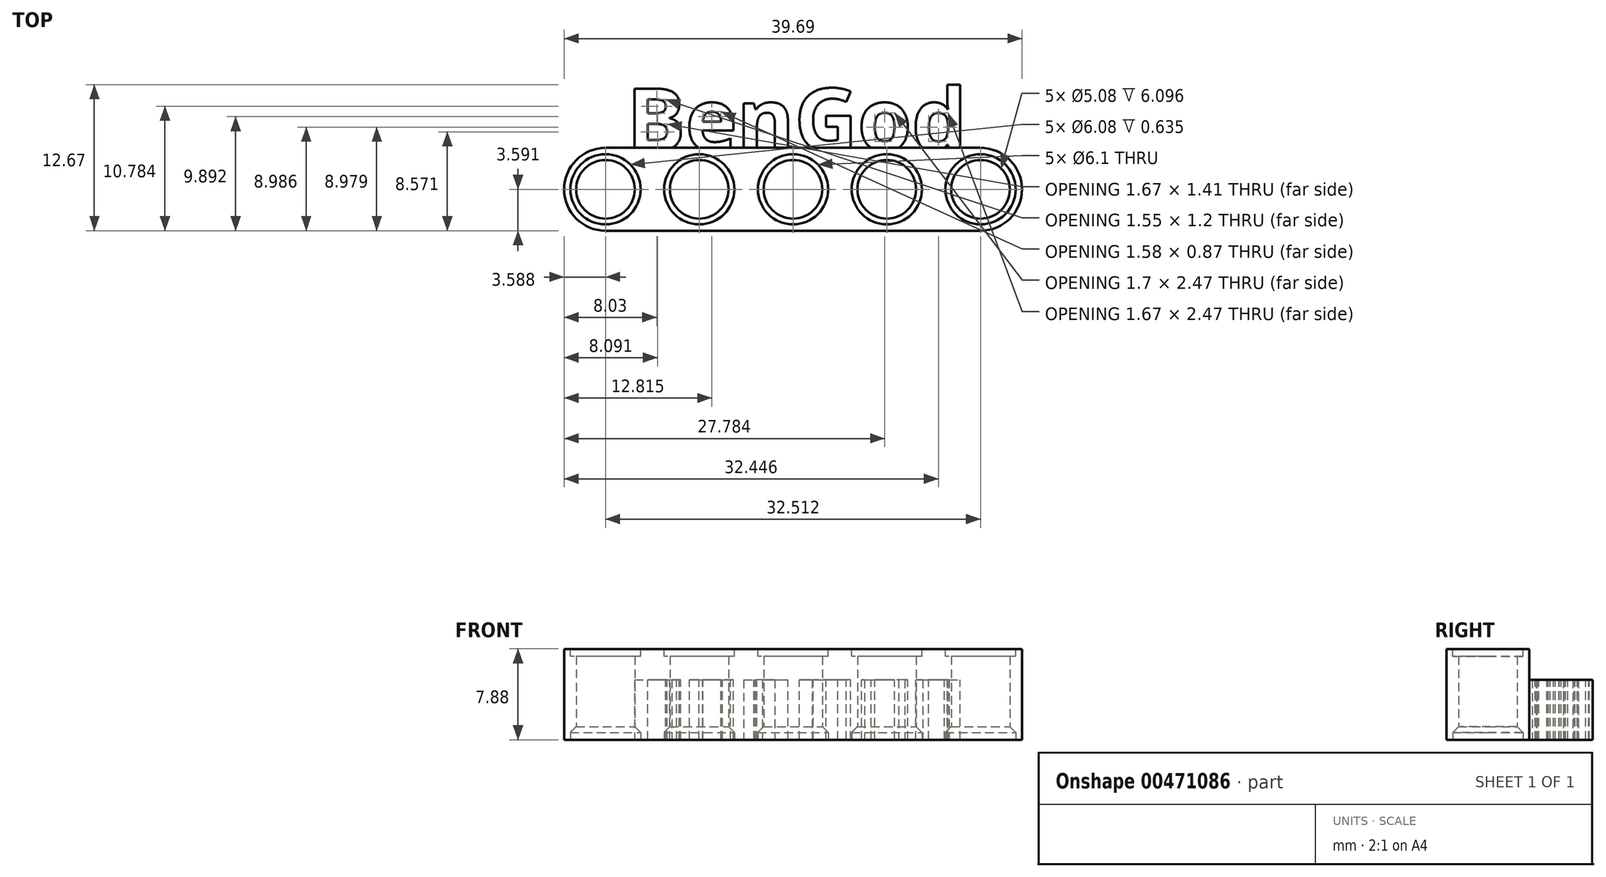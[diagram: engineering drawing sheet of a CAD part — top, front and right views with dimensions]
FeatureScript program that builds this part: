
annotation { "Feature Type Name" : "Feature", "Feature Type Description" : "" }
export const myFeature = defineFeature(function(context is Context, id is Id, definition is map)
    precondition{}
    {
        {
            var Q0;
            Q0=qCreatedBy(makeId("Top.planeOp"),FACE);
            var sketch = newSketch(context, id + "F0", { "sketchPlane" : qUnion([Q0])});
            skCircle(sketch, "E0", {"center": v(-60.84, 14.37) * mm, "radius": 3.6 * mm});
            skCircle(sketch, "E1.1.0.0", {"center": v(-52.71, 14.37) * mm, "radius": 3.6 * mm});
            skCircle(sketch, "E1.2.0.0", {"center": v(-44.59, 14.37) * mm, "radius": 3.6 * mm});
            skCircle(sketch, "E1.3.0.0", {"center": v(-36.46, 14.37) * mm, "radius": 3.6 * mm});
            skLineSegment(sketch, "E1.direction1", {"start": v(-60.84, 14.37) * mm, "end": v(-52.71, 14.37) * mm, "construction": true});
            skCircle(sketch, "E2.0.4.0", {"center": v(-28.33, 14.37) * mm, "radius": 3.6 * mm});
            skLineSegment(sketch, "E3.left", {"start": v(-60.84, 14.37) * mm, "end": v(-60.84, 14.37) * mm});
            skLineSegment(sketch, "E3.right", {"start": v(-28.33, 14.37) * mm, "end": v(-28.33, 14.37) * mm});
            skLineSegment(sketch, "E4.bottom", {"start": v(-60.84, 17.96) * mm, "end": v(-28.33, 17.96) * mm});
            skLineSegment(sketch, "E4.top", {"start": v(-60.84, 10.78) * mm, "end": v(-28.33, 10.78) * mm});
            skCircle(sketch, "E5", {"center": v(-60.84, 14.37) * mm, "radius": 3.05 * mm});
            skCircle(sketch, "E6.1.0.0", {"center": v(-52.71, 14.37) * mm, "radius": 3.05 * mm});
            skCircle(sketch, "E6.2.0.0", {"center": v(-44.59, 14.37) * mm, "radius": 3.05 * mm});
            skCircle(sketch, "E6.3.0.0", {"center": v(-36.46, 14.37) * mm, "radius": 3.05 * mm});
            skCircle(sketch, "E6.4.0.0", {"center": v(-28.33, 14.37) * mm, "radius": 3.05 * mm});
            skCircle(sketch, "E7", {"center": v(-60.84, 14.37) * mm, "radius": 2.54 * mm});
            skCircle(sketch, "E8.1.0.0", {"center": v(-52.71, 14.37) * mm, "radius": 2.54 * mm});
            skCircle(sketch, "E8.2.0.0", {"center": v(-44.59, 14.37) * mm, "radius": 2.54 * mm});
            skCircle(sketch, "E8.3.0.0", {"center": v(-36.46, 14.37) * mm, "radius": 2.54 * mm});
            skCircle(sketch, "E8.4.0.0", {"center": v(-28.33, 14.37) * mm, "radius": 2.54 * mm});
            skSolve(sketch);
        }
        {
            var Q0;
            Q0=makeQuery(id+"F0.imprint","IMPRINT",FACE,{"disambiguationData":[TD([[makeQuery(id+"F0.imprint","IMPRINT",EDGE,{"derivedFrom":sQuery(id+"F0.wireOp",EDGE,"E6.2.0.0")}),1.0]])]});
            var Q1;
            {var subQ0=sQuery(id+"F0.wireOp",EDGE,"E4.bottom");var subQ1=sQuery(id+"F0.wireOp",EDGE,"E0");var subQ2=makeQuery(id+"F0.imprint","INTERSECT",VERTEX,{"derivedFrom":[subQ1,subQ0]});Q1=makeQuery(id+"F0.imprint","IMPRINT",FACE,{"disambiguationData":[TD([[makeQuery(id+"F0.imprint","IMPRINT",EDGE,{"disambiguationData":[TD([[subQ2,1.0]])],"derivedFrom":subQ1}),-1.0]])]});}
            var Q2;
            {var subQ0=sQuery(id+"F0.wireOp",EDGE,"E4.bottom");var subQ1=sQuery(id+"F0.wireOp",EDGE,"E1.1.0.0");var subQ2=makeQuery(id+"F0.imprint","INTERSECT",VERTEX,{"derivedFrom":[subQ1,subQ0]});Q2=makeQuery(id+"F0.imprint","IMPRINT",FACE,{"disambiguationData":[TD([[makeQuery(id+"F0.imprint","IMPRINT",EDGE,{"disambiguationData":[TD([[subQ2,1.0]])],"derivedFrom":subQ1}),-1.0]])]});}
            var Q3;
            Q3=makeQuery(id+"F0.imprint","IMPRINT",FACE,{"disambiguationData":[TD([[makeQuery(id+"F0.imprint","IMPRINT",EDGE,{"derivedFrom":sQuery(id+"F0.wireOp",EDGE,"E6.2.0.0")}),-1.0]])]});
            var Q4;
            Q4=makeQuery(id+"F0.imprint","IMPRINT",FACE,{"disambiguationData":[TD([[makeQuery(id+"F0.imprint","IMPRINT",EDGE,{"derivedFrom":sQuery(id+"F0.wireOp",EDGE,"E6.1.0.0")}),-1.0]])]});
            var Q5;
            Q5=makeQuery(id+"F0.imprint","IMPRINT",FACE,{"disambiguationData":[TD([[makeQuery(id+"F0.imprint","IMPRINT",EDGE,{"derivedFrom":sQuery(id+"F0.wireOp",EDGE,"E6.3.0.0")}),-1.0]])]});
            var Q6;
            Q6=makeQuery(id+"F0.imprint","IMPRINT",FACE,{"disambiguationData":[TD([[makeQuery(id+"F0.imprint","IMPRINT",EDGE,{"derivedFrom":sQuery(id+"F0.wireOp",EDGE,"E6.3.0.0")}),1.0]])]});
            var Q7;
            {var subQ0=sQuery(id+"F0.wireOp",EDGE,"E4.bottom");var subQ1=sQuery(id+"F0.wireOp",EDGE,"E1.3.0.0");var subQ2=makeQuery(id+"F0.imprint","INTERSECT",VERTEX,{"derivedFrom":[subQ1,subQ0]});Q7=makeQuery(id+"F0.imprint","IMPRINT",FACE,{"disambiguationData":[TD([[makeQuery(id+"F0.imprint","IMPRINT",EDGE,{"disambiguationData":[TD([[subQ2,1.0]])],"derivedFrom":subQ1}),-1.0]])]});}
            var Q8;
            Q8=makeQuery(id+"F0.imprint","IMPRINT",FACE,{"disambiguationData":[TD([[makeQuery(id+"F0.imprint","IMPRINT",EDGE,{"derivedFrom":sQuery(id+"F0.wireOp",EDGE,"E6.4.0.0")}),-1.0]])]});
            var Q9;
            Q9=makeQuery(id+"F0.imprint","IMPRINT",FACE,{"disambiguationData":[TD([[makeQuery(id+"F0.imprint","IMPRINT",EDGE,{"derivedFrom":sQuery(id+"F0.wireOp",EDGE,"E6.1.0.0")}),1.0]])]});
            var Q10;
            {var subQ0=sQuery(id+"F0.wireOp",EDGE,"E4.bottom");var subQ1=sQuery(id+"F0.wireOp",EDGE,"E1.2.0.0");var subQ2=makeQuery(id+"F0.imprint","INTERSECT",VERTEX,{"derivedFrom":[subQ1,subQ0]});Q10=makeQuery(id+"F0.imprint","IMPRINT",FACE,{"disambiguationData":[TD([[makeQuery(id+"F0.imprint","IMPRINT",EDGE,{"disambiguationData":[TD([[subQ2,1.0]])],"derivedFrom":subQ1}),-1.0]])]});}
            var Q11;
            Q11=makeQuery(id+"F0.imprint","IMPRINT",FACE,{"disambiguationData":[TD([[makeQuery(id+"F0.imprint","IMPRINT",EDGE,{"derivedFrom":sQuery(id+"F0.wireOp",EDGE,"E6.4.0.0")}),1.0]])]});
            var Q12;
            Q12=makeQuery(id+"F0.imprint","IMPRINT",FACE,{"disambiguationData":[TD([[makeQuery(id+"F0.imprint","IMPRINT",EDGE,{"derivedFrom":sQuery(id+"F0.wireOp",EDGE,"E5")}),-1.0]])]});
            var Q13;
            Q13=makeQuery(id+"F0.imprint","IMPRINT",FACE,{"disambiguationData":[TD([[makeQuery(id+"F0.imprint","IMPRINT",EDGE,{"derivedFrom":sQuery(id+"F0.wireOp",EDGE,"E5")}),1.0]])]});
            extrude(context, id + "F1", {"entities" : qUnion([Q0, Q1, Q2, Q3, Q4, Q5, Q6, Q7, Q8, Q9, Q10, Q11, Q12, Q13]), "endBound" : BoundingType.SYMMETRIC, "depth" : 7.87 * mm});
        }
        {
            var Q0;
            Q0=makeQuery(id+"F1.opExtrude","CAP_FACE",FACE,{"disambiguationData":[OSD([sQuery(id+"F0.wireOp",EDGE,"E0"),sQuery(id+"F0.wireOp",EDGE,"E2.0.4.0"),sQuery(id+"F0.wireOp",EDGE,"E4.bottom"),sQuery(id+"F0.wireOp",EDGE,"E4.top"),sQuery(id+"F0.wireOp",EDGE,"E7"),sQuery(id+"F0.wireOp",EDGE,"E8.1.0.0"),sQuery(id+"F0.wireOp",EDGE,"E8.2.0.0"),sQuery(id+"F0.wireOp",EDGE,"E8.3.0.0"),sQuery(id+"F0.wireOp",EDGE,"E8.4.0.0")])],"isStart":false});
            var sketch = newSketch(context, id + "F2", { "sketchPlane" : qUnion([Q0])});
            skCircle(sketch, "E9", {"center": v(-28.33, 14.37) * mm, "radius": 3.04 * mm});
            skCircle(sketch, "E10.1.0.0", {"center": v(-36.46, 14.37) * mm, "radius": 3.04 * mm});
            skCircle(sketch, "E10.2.0.0", {"center": v(-44.59, 14.37) * mm, "radius": 3.04 * mm});
            skCircle(sketch, "E10.3.0.0", {"center": v(-52.71, 14.37) * mm, "radius": 3.04 * mm});
            skCircle(sketch, "E10.4.0.0", {"center": v(-60.84, 14.37) * mm, "radius": 3.04 * mm});
            skLineSegment(sketch, "E10.direction1", {"start": v(-28.33, 14.37) * mm, "end": v(-36.46, 14.37) * mm, "construction": true});
            skSolve(sketch);
        }
        {
            var Q0;
            Q0=qSketchRegion(id+"F2",true);
            extrude(context, id + "F3", {"entities" : qUnion([Q0]), "operationType" : NewBodyOperationType.REMOVE, "oppositeDirection" : true, "depth" : 0.64 * mm});
        }
        {
            var Q0;
            Q0=makeQuery(id+"F1.opExtrude","CAP_FACE",FACE,{"disambiguationData":[OSD([sQuery(id+"F0.wireOp",EDGE,"E0"),sQuery(id+"F0.wireOp",EDGE,"E2.0.4.0"),sQuery(id+"F0.wireOp",EDGE,"E4.bottom"),sQuery(id+"F0.wireOp",EDGE,"E4.top"),sQuery(id+"F0.wireOp",EDGE,"E7"),sQuery(id+"F0.wireOp",EDGE,"E8.1.0.0"),sQuery(id+"F0.wireOp",EDGE,"E8.2.0.0"),sQuery(id+"F0.wireOp",EDGE,"E8.3.0.0"),sQuery(id+"F0.wireOp",EDGE,"E8.4.0.0")])],"isStart":true});
            var sketch = newSketch(context, id + "F4", { "sketchPlane" : qUnion([Q0])});
            skCircle(sketch, "E11", {"center": v(-60.84, -14.37) * mm, "radius": 3.05 * mm});
            skCircle(sketch, "E12.1.0.0", {"center": v(-52.71, -14.37) * mm, "radius": 3.05 * mm});
            skCircle(sketch, "E12.2.0.0", {"center": v(-44.59, -14.37) * mm, "radius": 3.05 * mm});
            skCircle(sketch, "E12.3.0.0", {"center": v(-36.46, -14.37) * mm, "radius": 3.05 * mm});
            skCircle(sketch, "E12.4.0.0", {"center": v(-28.33, -14.37) * mm, "radius": 3.05 * mm});
            skLineSegment(sketch, "E12.direction1", {"start": v(-60.84, -14.37) * mm, "end": v(-52.71, -14.37) * mm, "construction": true});
            skSolve(sketch);
        }
        {
            var Q0;
            Q0=qSketchRegion(id+"F4",true);
            extrude(context, id + "F5", {"entities" : qUnion([Q0]), "operationType" : NewBodyOperationType.REMOVE, "oppositeDirection" : true, "depth" : 0.64 * mm});
        }
        {
            var Q0;
            Q0=qCreatedBy(makeId("Top.planeOp"),FACE);
            var sketch = newSketch(context, id + "F6", { "sketchPlane" : qUnion([Q0])});
            skText(sketch, "E13", { "text": "BenGod", "fontName": "OpenSans-Bold.ttf"});
            const initialGuessF6  = {"E13": [-0.059, 0.0177, 1, 0, 0.00545]};
            skSetInitialGuess(sketch, initialGuessF6);
            skSolve(sketch);
        }
        {
            var Q0;
            Q0=qSketchRegion(id+"F6",true);
            extrude(context, id + "F7", {"entities" : qUnion([Q0]), "operationType" : NewBodyOperationType.ADD, "oppositeDirection" : true, "depth" : 3.94 * mm});
        }
        {
            var Q0;
            Q0=makeQuery(id+"F5.boolean.opBoolean","INTERSECT",EDGE,{"derivedFrom":[makeQuery(id+"F1.opExtrude","SWEPT_FACE",FACE,{"disambiguationData":[OSD([sQuery(id+"F0.wireOp",EDGE,"E8.3.0.0")])]}),makeQuery(id+"F5.opExtrude","CAP_FACE",FACE,{"disambiguationData":[OSD([sQuery(id+"F4.wireOp",EDGE,"E12.3.0.0")])],"isStart":false})]});
            chamfer(context, id + "F8", {"entities" : qUnion([Q0]), "chamferType" : ChamferType.OFFSET_ANGLE, "width" : 0.5 * mm, "oppositeDirection" : false, "angle" : 45 * degree});
        }
        {
            var Q0;
            Q0=makeQuery(id+"F5.boolean.opBoolean","INTERSECT",EDGE,{"derivedFrom":[makeQuery(id+"F1.opExtrude","SWEPT_FACE",FACE,{"disambiguationData":[OSD([sQuery(id+"F0.wireOp",EDGE,"E8.2.0.0")])]}),makeQuery(id+"F5.opExtrude","CAP_FACE",FACE,{"disambiguationData":[OSD([sQuery(id+"F4.wireOp",EDGE,"E12.2.0.0")])],"isStart":false})]});
            var Q1;
            Q1=makeQuery(id+"F5.boolean.opBoolean","INTERSECT",EDGE,{"derivedFrom":[makeQuery(id+"F1.opExtrude","SWEPT_FACE",FACE,{"disambiguationData":[OSD([sQuery(id+"F0.wireOp",EDGE,"E8.1.0.0")])]}),makeQuery(id+"F5.opExtrude","CAP_FACE",FACE,{"disambiguationData":[OSD([sQuery(id+"F4.wireOp",EDGE,"E12.1.0.0")])],"isStart":false})]});
            var Q2;
            Q2=makeQuery(id+"F5.boolean.opBoolean","INTERSECT",EDGE,{"derivedFrom":[makeQuery(id+"F1.opExtrude","SWEPT_FACE",FACE,{"disambiguationData":[OSD([sQuery(id+"F0.wireOp",EDGE,"E7")])]}),makeQuery(id+"F5.opExtrude","CAP_FACE",FACE,{"disambiguationData":[OSD([sQuery(id+"F4.wireOp",EDGE,"E11")])],"isStart":false})]});
            var Q3;
            Q3=makeQuery(id+"F5.boolean.opBoolean","INTERSECT",EDGE,{"derivedFrom":[makeQuery(id+"F1.opExtrude","SWEPT_FACE",FACE,{"disambiguationData":[OSD([sQuery(id+"F0.wireOp",EDGE,"E8.4.0.0")])]}),makeQuery(id+"F5.opExtrude","CAP_FACE",FACE,{"disambiguationData":[OSD([sQuery(id+"F4.wireOp",EDGE,"E12.4.0.0")])],"isStart":false})]});
            chamfer(context, id + "F9", {"entities" : qUnion([Q0, Q1, Q2, Q3]), "chamferType" : ChamferType.OFFSET_ANGLE, "width" : 0.5 * mm, "oppositeDirection" : false, "angle" : 45 * degree});
        }
        {
            var Q0;
            Q0 = qSketchRegion(id + "F6", true);
            extrude(context, id + "F10", {"entities" : qUnion([Q0]), "operationType" : NewBodyOperationType.ADD, "endBound" : BoundingType.SYMMETRIC, "depth" : 2.54 * mm});
        }
    });
